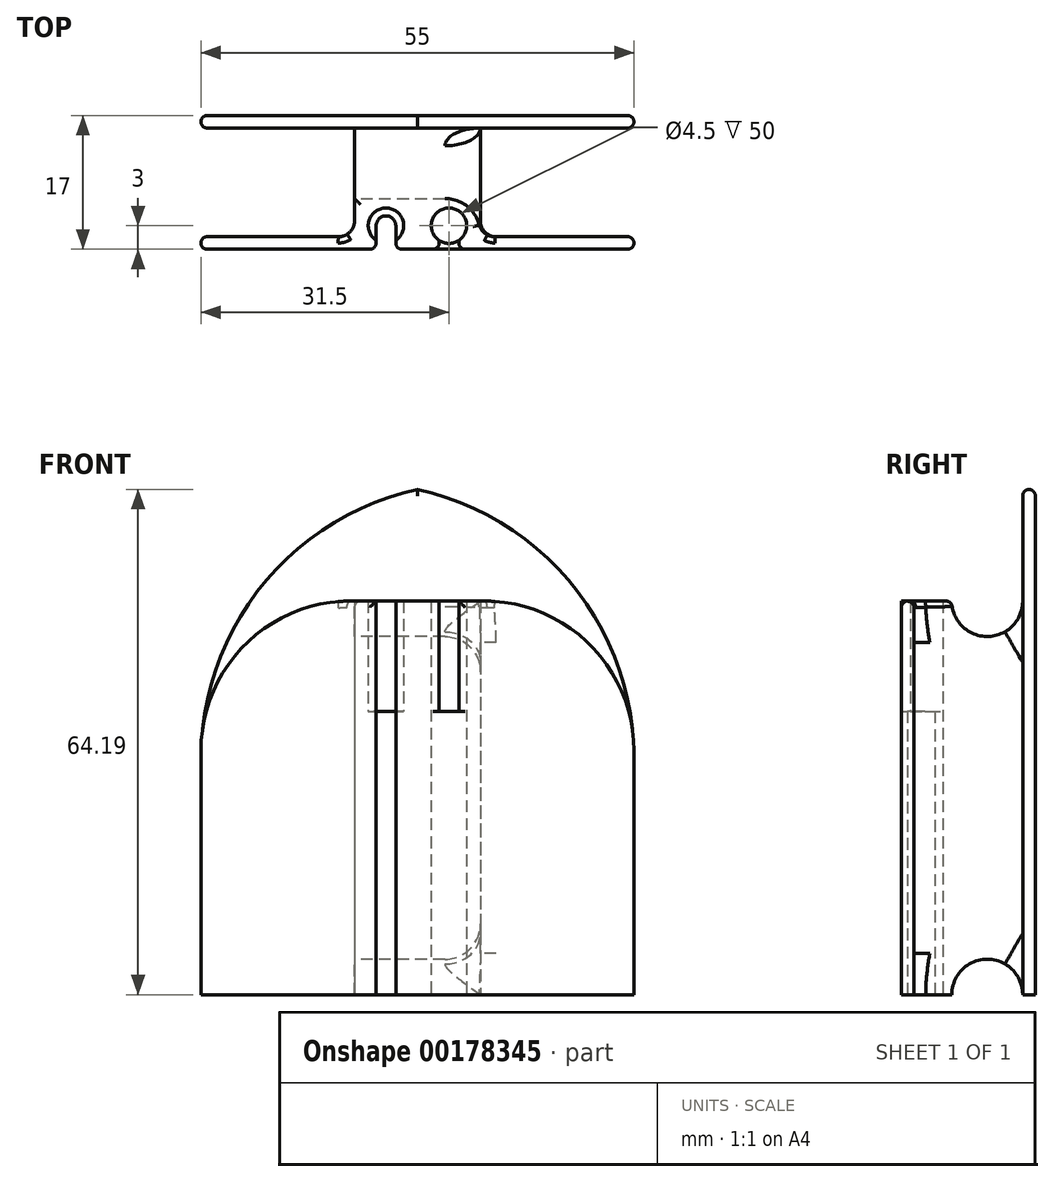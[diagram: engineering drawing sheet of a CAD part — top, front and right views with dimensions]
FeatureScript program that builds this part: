
annotation { "Feature Type Name" : "Feature", "Feature Type Description" : "" }
export const myFeature = defineFeature(function(context is Context, id is Id, definition is map)
    precondition{}
    {
        {
            var Q0;
            Q0=qCreatedBy(makeId("Top.planeOp"),FACE);
            var sketch = newSketch(context, id + "F0", { "sketchPlane" : qUnion([Q0])});
            skLineSegment(sketch, "E0", {"start": v(0, -8.5) * mm, "end": v(-27.5, -8.5) * mm});
            skLineSegment(sketch, "E1", {"start": v(-27.5, -8.5) * mm, "end": v(-27.5, -6.9) * mm});
            skLineSegment(sketch, "E2", {"start": v(-27.5, -6.9) * mm, "end": v(-8, -6.9) * mm});
            skLineSegment(sketch, "E3", {"start": v(-8, -6.9) * mm, "end": v(-8, 0) * mm});
            skLineSegment(sketch, "E4", {"start": v(0, 0) * mm, "end": v(0, -18.44) * mm, "construction": true});
            skLineSegment(sketch, "E5", {"start": v(0, 0) * mm, "end": v(-34.42, 0) * mm, "construction": true});
            skLineSegment(sketch, "E6.MirrorCS", {"start": v(0, -8.5) * mm, "end": v(27.5, -8.5) * mm});
            skLineSegment(sketch, "E7.MirrorCS", {"start": v(27.5, -6.9) * mm, "end": v(8, -6.9) * mm});
            skLineSegment(sketch, "E8.MirrorCS", {"start": v(27.5, -8.5) * mm, "end": v(27.5, -6.9) * mm});
            skLineSegment(sketch, "E9.MirrorCS", {"start": v(8, -6.9) * mm, "end": v(8, 0) * mm});
            skLineSegment(sketch, "E10.MirrorCS", {"start": v(-8, 6.9) * mm, "end": v(-8, 0) * mm});
            skLineSegment(sketch, "E11.MirrorCS", {"start": v(8, 6.9) * mm, "end": v(8, 0) * mm});
            skLineSegment(sketch, "E12.MirrorCS", {"start": v(27.5, 6.9) * mm, "end": v(8, 6.9) * mm});
            skLineSegment(sketch, "E13.MirrorCS", {"start": v(0, 8.5) * mm, "end": v(27.5, 8.5) * mm});
            skLineSegment(sketch, "E14.MirrorCS", {"start": v(0, 8.5) * mm, "end": v(-27.5, 8.5) * mm});
            skLineSegment(sketch, "E15.MirrorCS", {"start": v(-27.5, 8.5) * mm, "end": v(-27.5, 6.9) * mm});
            skLineSegment(sketch, "E16.MirrorCS", {"start": v(-27.5, 6.9) * mm, "end": v(-8, 6.9) * mm});
            skLineSegment(sketch, "E17.MirrorCS", {"start": v(27.5, 8.5) * mm, "end": v(27.5, 6.9) * mm});
            skCircle(sketch, "E18", {"center": v(-4, -5.5) * mm, "radius": 2.25 * mm});
            skCircle(sketch, "E19.MirrorC", {"center": v(4, -5.5) * mm, "radius": 2.25 * mm});
            skLineSegment(sketch, "E20", {"start": v(-8, 6.9) * mm, "end": v(8, 6.9) * mm});
            skCircle(sketch, "E21", {"center": v(-4, -5.5) * mm, "radius": 1.25 * mm});
            skCircle(sketch, "E22.MirrorC", {"center": v(4, -5.5) * mm, "radius": 1.25 * mm});
            skLineSegment(sketch, "E23", {"start": v(-2.75, -5.5) * mm, "end": v(-2.75, -8.5) * mm});
            skLineSegment(sketch, "E24", {"start": v(-5.25, -5.5) * mm, "end": v(-5.25, -8.5) * mm});
            skLineSegment(sketch, "E25.MirrorCS", {"start": v(2.75, -5.5) * mm, "end": v(2.75, -8.5) * mm});
            skLineSegment(sketch, "E26.MirrorCS", {"start": v(5.25, -5.5) * mm, "end": v(5.25, -8.5) * mm});
            skSolve(sketch);
        }
        {
            var Q0;
            {var subQ17=sQuery(id+"F0.wireOp",EDGE,"E1");Q0=makeQuery(id+"F0.imprint","IMPRINT",FACE,{"disambiguationData":[TD([[makeQuery(id+"F0.imprint","IMPRINT",EDGE,{"derivedFrom":subQ17}),-1.0]])]});}
            extrude(context, id + "F1", {"entities" : qUnion([Q0]), "depth" : 50 * mm});
        }
        {
            var Q0;
            Q0=makeQuery(id+"F0.imprint","IMPRINT",FACE,{"disambiguationData":[TD([[makeQuery(id+"F0.imprint","IMPRINT",EDGE,{"derivedFrom":sQuery(id+"F0.wireOp",EDGE,"E12.MirrorCS")}),-1.0]])]});
            extrude(context, id + "F2", {"entities" : qUnion([Q0]), "operationType" : NewBodyOperationType.ADD, "depth" : 65 * mm});
        }
        {
            var Q0;
            {var subQ0=sQuery(id+"F0.wireOp",EDGE,"E25.MirrorCS");var subQ1=sQuery(id+"F0.wireOp",EDGE,"E19.MirrorC");var subQ2=makeQuery(id+"F0.imprint","INTERSECT",VERTEX,{"derivedFrom":[subQ1,subQ0]});Q0=makeQuery(id+"F0.imprint","IMPRINT",FACE,{"disambiguationData":[TD([[makeQuery(id+"F0.imprint","IMPRINT",EDGE,{"disambiguationData":[TD([[subQ2,-1.0]])],"derivedFrom":subQ1}),-1.0]])]});}
            var Q1;
            {var subQ0=sQuery(id+"F0.wireOp",EDGE,"E23");var subQ1=sQuery(id+"F0.wireOp",EDGE,"E18");var subQ2=makeQuery(id+"F0.imprint","INTERSECT",VERTEX,{"derivedFrom":[subQ1,subQ0]});Q1=makeQuery(id+"F0.imprint","IMPRINT",FACE,{"disambiguationData":[TD([[makeQuery(id+"F0.imprint","IMPRINT",EDGE,{"disambiguationData":[TD([[subQ2,-1.0]])],"derivedFrom":subQ1}),1.0]])]});}
            extrude(context, id + "F3", {"entities" : qUnion([Q0, Q1]), "operationType" : NewBodyOperationType.ADD, "depth" : 36 * mm});
        }
        {
            var Q0;
            Q0=makeQuery(id+"F1.opExtrude","CAP_EDGE",EDGE,{"disambiguationData":[OSD([sQuery(id+"F0.wireOp",EDGE,"E1")])],"isStart":false});
            var Q1;
            Q1=makeQuery(id+"F1.opExtrude","CAP_EDGE",EDGE,{"disambiguationData":[OSD([sQuery(id+"F0.wireOp",EDGE,"E8.MirrorCS")])],"isStart":false});
            fillet(context, id + "F4", {"entities" : qUnion([Q0, Q1]), "radius" : 19 * mm, "tangentPropagation" : true, "allowEdgeOverflow" : false});
        }
        {
            var Q0;
            Q0=makeQuery(id+"F1.opExtrude","SWEPT_FACE",FACE,{"disambiguationData":[OSD([sQuery(id+"F0.wireOp",EDGE,"E3"),sQuery(id+"F0.wireOp",EDGE,"E10.MirrorCS")])]});
            var sketch = newSketch(context, id + "F5", { "sketchPlane" : qUnion([Q0])});
            skArc(sketch, "E27", {"start": v(-6.9, 50) * mm, "mid": v(-2.4, 45.5) * mm, "end": v(2.1, 50) * mm});
            skArc(sketch, "E28", {"start": v(2.1, 0) * mm, "mid": v(-2.4, 4.5) * mm, "end": v(-6.9, 0) * mm});
            skSolve(sketch);
        }
        {
            var Q0;
            {var subQ0=sQuery(id+"F5.wireOp",EDGE,"E28");Q0=makeQuery(id+"F5.imprint","IMPRINT",FACE,{"disambiguationData":[TD([[makeQuery(id+"F5.imprint","IMPRINT",EDGE,{"derivedFrom":subQ0}),1.0]])]});}
            var Q1;
            {var subQ0=sQuery(id+"F5.wireOp",EDGE,"E27");Q1=makeQuery(id+"F5.imprint","IMPRINT",FACE,{"disambiguationData":[TD([[makeQuery(id+"F5.imprint","IMPRINT",EDGE,{"derivedFrom":subQ0}),1.0]])]});}
            extrude(context, id + "F6", {"entities" : qUnion([Q0, Q1]), "operationType" : NewBodyOperationType.REMOVE, "endBound" : BoundingType.THROUGH_ALL, "oppositeDirection" : true, "depth" : 25 * mm});
        }
        {
            var Q0;
            Q0=makeQuery(id+"F6.boolean.opBoolean","INTERSECT",EDGE,{"derivedFrom":[makeQuery(id+"F1.opExtrude","SWEPT_FACE",FACE,{"disambiguationData":[OSD([sQuery(id+"F0.wireOp",EDGE,"E9.MirrorCS"),sQuery(id+"F0.wireOp",EDGE,"E11.MirrorCS")])]}),makeQuery(id+"F6.opExtrude","SWEPT_FACE",FACE,{"disambiguationData":[OSD([sQuery(id+"F5.wireOp",EDGE,"E27")])]})]});
            var Q1;
            Q1=makeQuery(id+"F6.boolean.opBoolean","COPY",EDGE,{"derivedFrom":makeQuery(id+"F6.opExtrude","CAP_EDGE",EDGE,{"disambiguationData":[OSD([sQuery(id+"F5.wireOp",EDGE,"E27")])],"isStart":true})});
            var Q2;
            Q2=makeQuery(id+"F6.boolean.opBoolean","INTERSECT",EDGE,{"derivedFrom":[makeQuery(id+"F1.opExtrude","SWEPT_FACE",FACE,{"disambiguationData":[OSD([sQuery(id+"F0.wireOp",EDGE,"E9.MirrorCS"),sQuery(id+"F0.wireOp",EDGE,"E11.MirrorCS")])]}),makeQuery(id+"F6.opExtrude","SWEPT_FACE",FACE,{"disambiguationData":[OSD([sQuery(id+"F5.wireOp",EDGE,"E28")])]})]});
            var Q3;
            Q3=makeQuery(id+"F6.boolean.opBoolean","COPY",EDGE,{"derivedFrom":makeQuery(id+"F6.opExtrude","CAP_EDGE",EDGE,{"disambiguationData":[OSD([sQuery(id+"F5.wireOp",EDGE,"E28")])],"isStart":true})});
            fillet(context, id + "F7", {"entities" : qUnion([Q0, Q1, Q2, Q3]), "radius" : 4.5 * mm, "tangentPropagation" : true, "allowEdgeOverflow" : false});
        }
        {
            var Q0;
            Q0=makeQuery(id+"F2.opExtrude","CAP_EDGE",EDGE,{"disambiguationData":[OSD([sQuery(id+"F0.wireOp",EDGE,"E15.MirrorCS")])],"isStart":false});
            var Q1;
            Q1=makeQuery(id+"F2.opExtrude","CAP_EDGE",EDGE,{"disambiguationData":[OSD([sQuery(id+"F0.wireOp",EDGE,"E17.MirrorCS")])],"isStart":false});
            fillet(context, id + "F8", {"entities" : qUnion([Q0, Q1]), "radius" : 35 * mm, "tangentPropagation" : true, "allowEdgeOverflow" : false});
        }
        {
            var Q0;
            Q0=makeQuery(id+"F1.opExtrude","SWEPT_EDGE",EDGE,{"disambiguationData":[OSD([sQuery(id+"F0.wireOp",EDGE,"E11.MirrorCS"),sQuery(id+"F0.wireOp",EDGE,"E12.MirrorCS"),sQuery(id+"F0.wireOp",EDGE,"E20")])]});
            var Q1;
            Q1=makeQuery(id+"F1.opExtrude","SWEPT_EDGE",EDGE,{"disambiguationData":[OSD([sQuery(id+"F0.wireOp",EDGE,"E7.MirrorCS"),sQuery(id+"F0.wireOp",EDGE,"E9.MirrorCS")])]});
            var Q2;
            Q2=makeQuery(id+"F1.opExtrude","SWEPT_EDGE",EDGE,{"disambiguationData":[OSD([sQuery(id+"F0.wireOp",EDGE,"E2"),sQuery(id+"F0.wireOp",EDGE,"E3")])]});
            var Q3;
            Q3=makeQuery(id+"F1.opExtrude","SWEPT_EDGE",EDGE,{"disambiguationData":[OSD([sQuery(id+"F0.wireOp",EDGE,"E10.MirrorCS"),sQuery(id+"F0.wireOp",EDGE,"E16.MirrorCS"),sQuery(id+"F0.wireOp",EDGE,"E20")])]});
            fillet(context, id + "F9", {"entities" : qUnion([Q0, Q1, Q2, Q3]), "radius" : 2 * mm, "tangentPropagation" : true, "allowEdgeOverflow" : false});
        }
        {
            var Q0;
            Q0=makeQuery(id+"F4.opFillet","BLEND_EDGE",EDGE,{"blendedFrom":[makeQuery(id+"F1.opExtrude","CAP_EDGE",EDGE,{"disambiguationData":[OSD([sQuery(id+"F0.wireOp",EDGE,"E1")])],"isStart":false}),makeQuery(id+"F1.opExtrude","SWEPT_FACE",FACE,{"disambiguationData":[OSD([sQuery(id+"F0.wireOp",EDGE,"E0")])]})],"blendedInto":[makeQuery(id+"F1.opExtrude","SWEPT_FACE",FACE,{"disambiguationData":[OSD([sQuery(id+"F0.wireOp",EDGE,"E0")])]})]});
            var Q1;
            Q1=makeQuery(id+"F4.opFillet","BLEND_EDGE",EDGE,{"blendedFrom":[makeQuery(id+"F1.opExtrude","CAP_EDGE",EDGE,{"disambiguationData":[OSD([sQuery(id+"F0.wireOp",EDGE,"E8.MirrorCS")])],"isStart":false}),makeQuery(id+"F1.opExtrude","SWEPT_FACE",FACE,{"disambiguationData":[OSD([sQuery(id+"F0.wireOp",EDGE,"E6.MirrorCS")])]})],"blendedInto":[makeQuery(id+"F1.opExtrude","SWEPT_FACE",FACE,{"disambiguationData":[OSD([sQuery(id+"F0.wireOp",EDGE,"E6.MirrorCS")])]})]});
            var Q2;
            Q2=makeQuery(id+"F4.opFillet","BLEND_EDGE",EDGE,{"blendedFrom":[makeQuery(id+"F1.opExtrude","CAP_EDGE",EDGE,{"disambiguationData":[OSD([sQuery(id+"F0.wireOp",EDGE,"E8.MirrorCS")])],"isStart":false}),makeQuery(id+"F1.opExtrude","SWEPT_FACE",FACE,{"disambiguationData":[OSD([sQuery(id+"F0.wireOp",EDGE,"E7.MirrorCS")])]})],"blendedInto":[makeQuery(id+"F1.opExtrude","SWEPT_FACE",FACE,{"disambiguationData":[OSD([sQuery(id+"F0.wireOp",EDGE,"E7.MirrorCS")])]})]});
            var Q3;
            Q3=makeQuery(id+"F4.opFillet","BLEND_EDGE",EDGE,{"blendedFrom":[makeQuery(id+"F1.opExtrude","CAP_EDGE",EDGE,{"disambiguationData":[OSD([sQuery(id+"F0.wireOp",EDGE,"E1")])],"isStart":false}),makeQuery(id+"F1.opExtrude","SWEPT_FACE",FACE,{"disambiguationData":[OSD([sQuery(id+"F0.wireOp",EDGE,"E2")])]})],"blendedInto":[makeQuery(id+"F1.opExtrude","SWEPT_FACE",FACE,{"disambiguationData":[OSD([sQuery(id+"F0.wireOp",EDGE,"E2")])]})]});
            var Q4;
            Q4=makeQuery(id+"F8.opFillet","BLEND_EDGE",EDGE,{"blendedFrom":[makeQuery(id+"F2.opExtrude","CAP_EDGE",EDGE,{"disambiguationData":[OSD([sQuery(id+"F0.wireOp",EDGE,"E15.MirrorCS")])],"isStart":false}),makeQuery(id+"F2.opExtrude","SWEPT_FACE",FACE,{"disambiguationData":[OSD([sQuery(id+"F0.wireOp",EDGE,"E13.MirrorCS"),sQuery(id+"F0.wireOp",EDGE,"E14.MirrorCS")])]})],"blendedInto":[makeQuery(id+"F2.opExtrude","SWEPT_FACE",FACE,{"disambiguationData":[OSD([sQuery(id+"F0.wireOp",EDGE,"E13.MirrorCS"),sQuery(id+"F0.wireOp",EDGE,"E14.MirrorCS")])]})]});
            var Q5;
            Q5=makeQuery(id+"F8.opFillet","BLEND_EDGE",EDGE,{"blendedFrom":[makeQuery(id+"F2.opExtrude","CAP_EDGE",EDGE,{"disambiguationData":[OSD([sQuery(id+"F0.wireOp",EDGE,"E17.MirrorCS")])],"isStart":false}),makeQuery(id+"F2.opExtrude","SWEPT_FACE",FACE,{"disambiguationData":[OSD([sQuery(id+"F0.wireOp",EDGE,"E13.MirrorCS"),sQuery(id+"F0.wireOp",EDGE,"E14.MirrorCS")])]})],"blendedInto":[makeQuery(id+"F2.opExtrude","SWEPT_FACE",FACE,{"disambiguationData":[OSD([sQuery(id+"F0.wireOp",EDGE,"E13.MirrorCS"),sQuery(id+"F0.wireOp",EDGE,"E14.MirrorCS")])]})]});
            var Q6;
            Q6=makeQuery(id+"F8.opFillet","BLEND_EDGE",EDGE,{"blendedFrom":[makeQuery(id+"F2.opExtrude","CAP_EDGE",EDGE,{"disambiguationData":[OSD([sQuery(id+"F0.wireOp",EDGE,"E17.MirrorCS")])],"isStart":false}),makeQuery(id+"F2.opExtrude","SWEPT_FACE",FACE,{"disambiguationData":[OSD([sQuery(id+"F0.wireOp",EDGE,"E12.MirrorCS"),sQuery(id+"F0.wireOp",EDGE,"E16.MirrorCS"),sQuery(id+"F0.wireOp",EDGE,"E20")])]})],"blendedInto":[makeQuery(id+"F2.opExtrude","SWEPT_FACE",FACE,{"disambiguationData":[OSD([sQuery(id+"F0.wireOp",EDGE,"E12.MirrorCS"),sQuery(id+"F0.wireOp",EDGE,"E16.MirrorCS"),sQuery(id+"F0.wireOp",EDGE,"E20")])]})]});
            var Q7;
            Q7=makeQuery(id+"F8.opFillet","BLEND_EDGE",EDGE,{"blendedFrom":[makeQuery(id+"F2.opExtrude","CAP_EDGE",EDGE,{"disambiguationData":[OSD([sQuery(id+"F0.wireOp",EDGE,"E15.MirrorCS")])],"isStart":false}),makeQuery(id+"F2.opExtrude","SWEPT_FACE",FACE,{"disambiguationData":[OSD([sQuery(id+"F0.wireOp",EDGE,"E12.MirrorCS"),sQuery(id+"F0.wireOp",EDGE,"E16.MirrorCS"),sQuery(id+"F0.wireOp",EDGE,"E20")])]})],"blendedInto":[makeQuery(id+"F2.opExtrude","SWEPT_FACE",FACE,{"disambiguationData":[OSD([sQuery(id+"F0.wireOp",EDGE,"E12.MirrorCS"),sQuery(id+"F0.wireOp",EDGE,"E16.MirrorCS"),sQuery(id+"F0.wireOp",EDGE,"E20")])]})]});
            var Q8;
            Q8=makeQuery(id+"F1.opExtrude","SWEPT_EDGE",EDGE,{"disambiguationData":[OSD([sQuery(id+"F0.wireOp",EDGE,"E0"),sQuery(id+"F0.wireOp",EDGE,"E24")])]});
            var Q9;
            Q9=makeQuery(id+"F1.opExtrude","SWEPT_EDGE",EDGE,{"disambiguationData":[OSD([sQuery(id+"F0.wireOp",EDGE,"E6.MirrorCS"),sQuery(id+"F0.wireOp",EDGE,"E26.MirrorCS")])]});
            var Q10;
            Q10=makeQuery(id+"F1.opExtrude","SWEPT_EDGE",EDGE,{"disambiguationData":[OSD([sQuery(id+"F0.wireOp",EDGE,"E0"),sQuery(id+"F0.wireOp",EDGE,"E23")])]});
            var Q11;
            Q11=makeQuery(id+"F1.opExtrude","SWEPT_EDGE",EDGE,{"disambiguationData":[OSD([sQuery(id+"F0.wireOp",EDGE,"E6.MirrorCS"),sQuery(id+"F0.wireOp",EDGE,"E25.MirrorCS")])]});
            fillet(context, id + "F10", {"entities" : qUnion([Q0, Q1, Q2, Q3, Q4, Q5, Q6, Q7, Q8, Q9, Q10, Q11]), "radius" : 0.8 * mm, "tangentPropagation" : true, "allowEdgeOverflow" : false});
        }
    });
